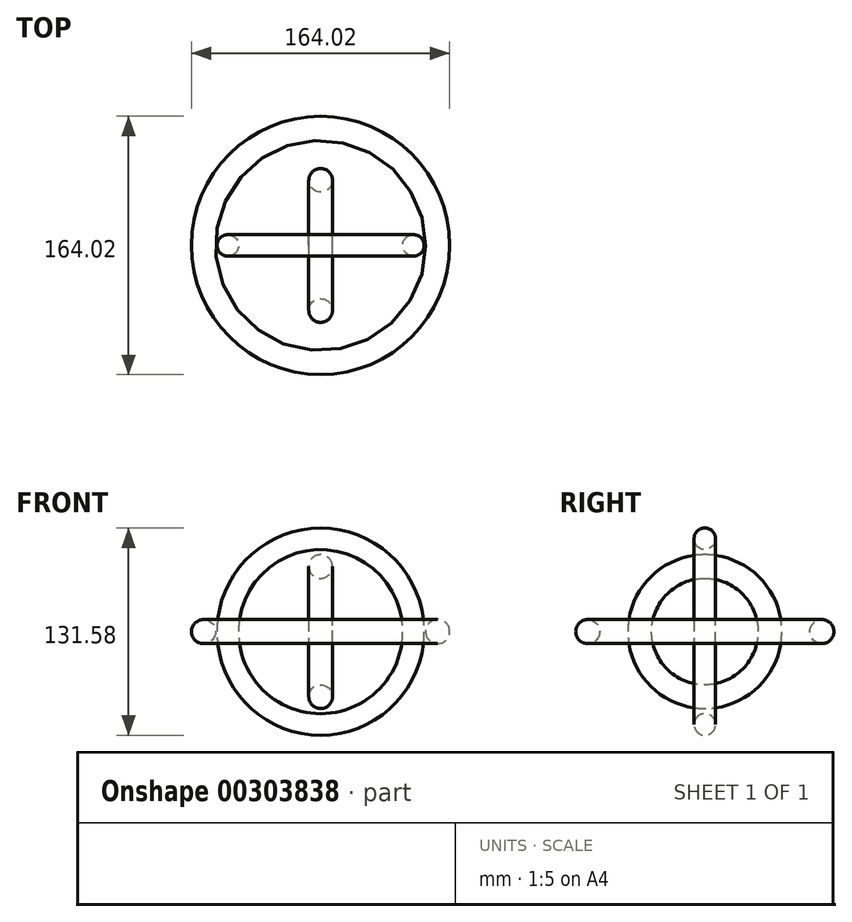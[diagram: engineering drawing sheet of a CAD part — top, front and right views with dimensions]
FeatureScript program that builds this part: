
annotation { "Feature Type Name" : "Feature", "Feature Type Description" : "" }
export const myFeature = defineFeature(function(context is Context, id is Id, definition is map)
    precondition{}
    {
        {
            var Q0;
            Q0=qCreatedBy(makeId("Front.planeOp"),FACE);
            var sketch = newSketch(context, id + "F0", { "sketchPlane" : qUnion([Q0])});
            skCircle(sketch, "E0", {"center": v(-74.37, 0) * mm, "radius": 7.64 * mm});
            skLineSegment(sketch, "E1", {"start": v(-66.72, 0) * mm, "end": v(0, 0) * mm});
            skLineSegment(sketch, "E2", {"start": v(0, 24.14) * mm, "end": v(0, -26.66) * mm});
            skSolve(sketch);
        }
        {
            var Q0;
            Q0=makeQuery(id+"F0.imprint","IMPRINT",FACE,{"disambiguationData":[TD([[makeQuery(id+"F0.imprint","IMPRINT",EDGE,{"derivedFrom":sQuery(id+"F0.wireOp",EDGE,"E0")}),1.0]])]});
            var Q1;
            Q1=sQuery(id+"F0.wireOp",EDGE,"E2");
            revolve(context, id + "F1", {"entities" : qUnion([Q0]), "axis" : qUnion([Q1]), "revolveType" : RevolveType.FULL});
        }
        {
            var Q0;
            Q0=qCreatedBy(makeId("Top.planeOp"),FACE);
            var sketch = newSketch(context, id + "F2", { "sketchPlane" : qUnion([Q0])});
            skCircle(sketch, "E3", {"center": v(-58.96, 0) * mm, "radius": 6.83 * mm});
            skLineSegment(sketch, "E4", {"start": v(0, -22.7) * mm, "end": v(0, 19.3) * mm});
            skSolve(sketch);
        }
        {
            var Q0;
            Q0=makeQuery(id+"F2.imprint","IMPRINT",FACE,{"disambiguationData":[TD([[makeQuery(id+"F2.imprint","IMPRINT",EDGE,{"derivedFrom":sQuery(id+"F2.wireOp",EDGE,"E3")}),1.0]])]});
            var Q1;
            Q1=sQuery(id+"F2.wireOp",EDGE,"E4");
            revolve(context, id + "F3", {"entities" : qUnion([Q0]), "axis" : qUnion([Q1]), "revolveType" : RevolveType.FULL});
        }
        {
            var Q0;
            Q0=qCreatedBy(makeId("Top.planeOp"),FACE);
            var sketch = newSketch(context, id + "F4", { "sketchPlane" : qUnion([Q0])});
            skPoint(sketch, "E5.center.orphan", {"position": v(57.52, 0) * mm});
            skLineSegment(sketch, "E6", {"start": v(0, 24.12) * mm, "end": v(0, -18.66) * mm});
            skPoint(sketch, "E7.center.orphan", {"position": v(47.66, 0) * mm});
            skCircle(sketch, "E8", {"center": v(0, 41.34) * mm, "radius": 7.53 * mm});
            skLineSegment(sketch, "E9", {"start": v(-17.06, 0) * mm, "end": v(18.66, 0) * mm});
            skSolve(sketch);
        }
        {
            var Q0;
            Q0=makeQuery(id+"F4.imprint","IMPRINT",FACE,{"disambiguationData":[TD([[makeQuery(id+"F4.imprint","IMPRINT",EDGE,{"derivedFrom":sQuery(id+"F4.wireOp",EDGE,"E8")}),1.0]])]});
            var Q1;
            Q1=sQuery(id+"F4.wireOp",EDGE,"E9");
            revolve(context, id + "F5", {"entities" : qUnion([Q0]), "axis" : qUnion([Q1]), "revolveType" : RevolveType.FULL});
        }
    });
